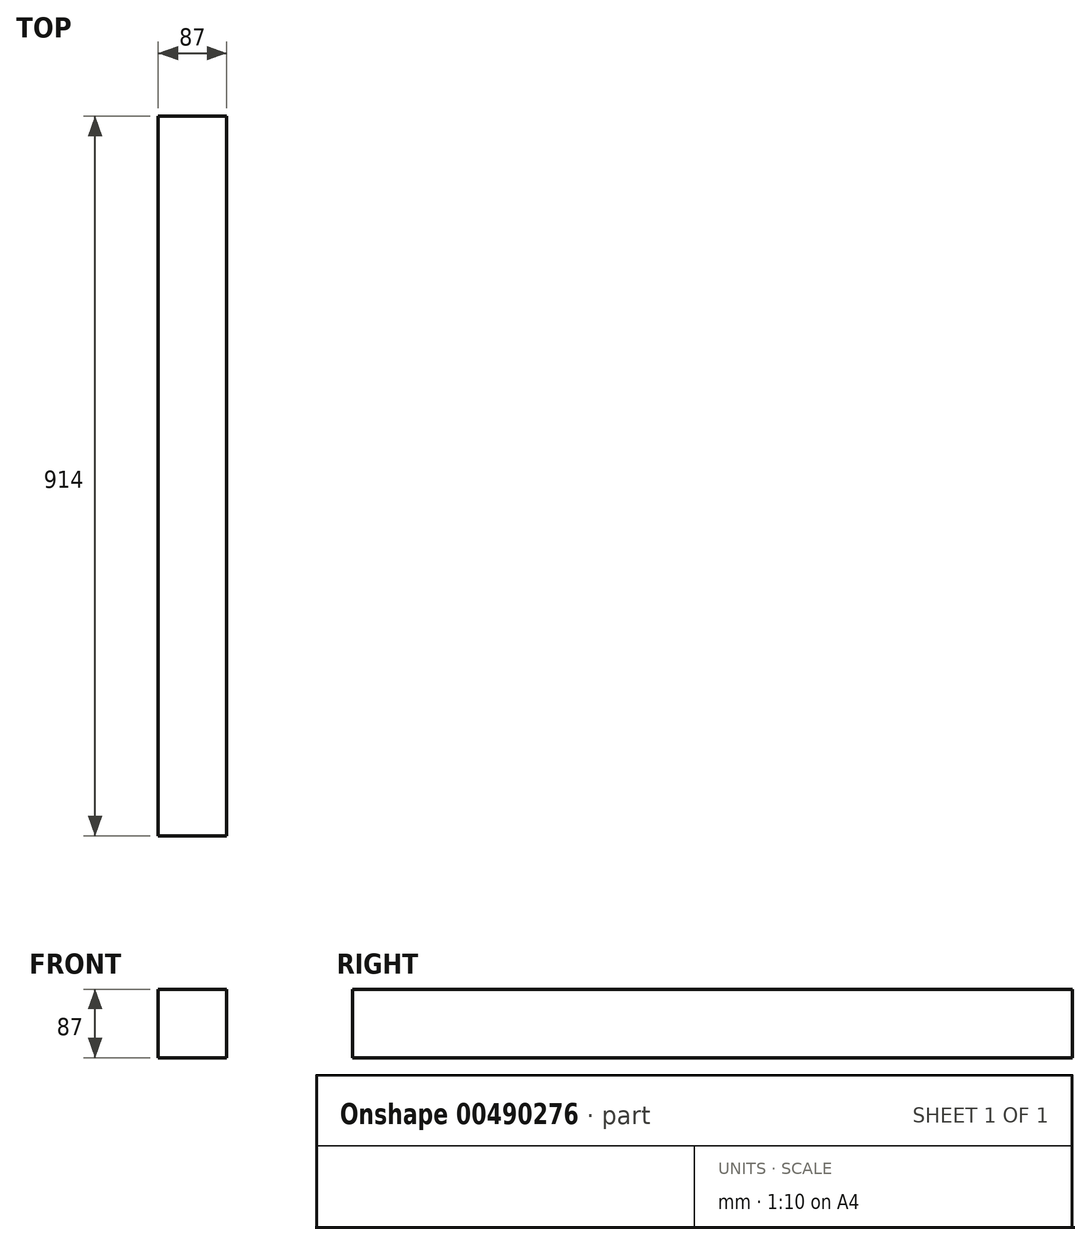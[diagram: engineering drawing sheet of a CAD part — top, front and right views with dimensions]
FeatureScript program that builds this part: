
annotation { "Feature Type Name" : "Feature", "Feature Type Description" : "" }
export const myFeature = defineFeature(function(context is Context, id is Id, definition is map)
    precondition{}
    {
        {
            var Q0;
            Q0=qCreatedBy(makeId("Front.planeOp"),FACE);
            var sketch = newSketch(context, id + "F0", { "sketchPlane" : qUnion([Q0])});
            skLineSegment(sketch, "E0.bottom", {"start": v(43.5, 43.5) * mm, "end": v(-43.5, 43.5) * mm});
            skLineSegment(sketch, "E0.top", {"start": v(43.5, -43.5) * mm, "end": v(-43.5, -43.5) * mm});
            skLineSegment(sketch, "E0.left", {"start": v(43.5, 43.5) * mm, "end": v(43.5, -43.5) * mm});
            skLineSegment(sketch, "E0.right", {"start": v(-43.5, 43.5) * mm, "end": v(-43.5, -43.5) * mm});
            skPoint(sketch, "E0.middle", {"position": v(0, 0) * mm});
            skSolve(sketch);
        }
        {
            var Q0;
            Q0=makeQuery(id+"F0.imprint","IMPRINT",FACE,{"disambiguationData":[TD([[makeQuery(id+"F0.imprint","IMPRINT",EDGE,{"derivedFrom":sQuery(id+"F0.wireOp",EDGE,"E0.bottom")}),1.0]])]});
            extrude(context, id + "F1", {"entities" : qUnion([Q0]), "depth" : 914 * mm});
        }
    });
